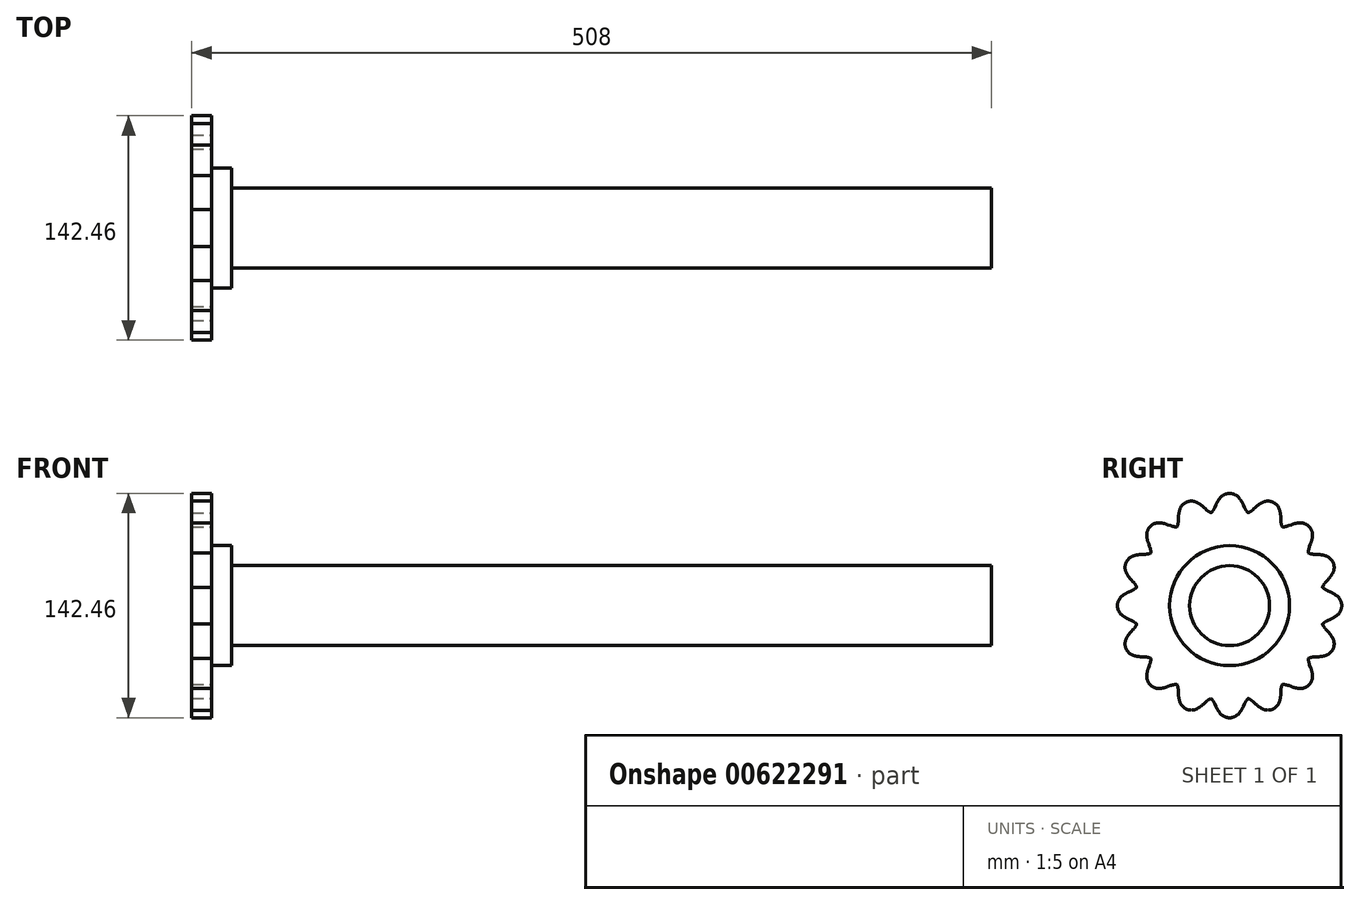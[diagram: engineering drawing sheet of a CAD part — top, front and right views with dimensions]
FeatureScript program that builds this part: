
annotation { "Feature Type Name" : "Feature", "Feature Type Description" : "" }
export const myFeature = defineFeature(function(context is Context, id is Id, definition is map)
    precondition{}
    {
        {
            var Q0;
            Q0=qCreatedBy(makeId("Front.planeOp"),FACE);
            var sketch = newSketch(context, id + "F0", { "sketchPlane" : qUnion([Q0])});
            skLineSegment(sketch, "E0", {"start": v(0, 0) * mm, "end": v(55.03, 0) * mm, "construction": true});
            skLineSegment(sketch, "E1.bottom", {"start": v(0, 25.4) * mm, "end": v(12.7, 25.4) * mm});
            skLineSegment(sketch, "E1.top", {"start": v(0, 76.2) * mm, "end": v(12.7, 76.2) * mm});
            skLineSegment(sketch, "E1.left", {"start": v(0, 25.4) * mm, "end": v(0, 76.2) * mm});
            skLineSegment(sketch, "E1.right", {"start": v(12.7, 25.4) * mm, "end": v(12.7, 76.2) * mm});
            skLineSegment(sketch, "E2.MirrorCS", {"start": v(12.7, -25.4) * mm, "end": v(12.7, -76.2) * mm});
            skLineSegment(sketch, "E3.MirrorCS", {"start": v(0, -25.4) * mm, "end": v(0, -76.2) * mm});
            skLineSegment(sketch, "E4.MirrorCS", {"start": v(0, -76.2) * mm, "end": v(12.7, -76.2) * mm});
            skLineSegment(sketch, "E5.MirrorCS", {"start": v(0, -25.4) * mm, "end": v(12.7, -25.4) * mm});
            skLineSegment(sketch, "E6.bottom", {"start": v(0, 38.1) * mm, "end": v(25.4, 38.1) * mm});
            skLineSegment(sketch, "E6.top", {"start": v(0, 25.4) * mm, "end": v(25.4, 25.4) * mm});
            skLineSegment(sketch, "E6.left", {"start": v(0, 38.1) * mm, "end": v(0, 25.4) * mm});
            skLineSegment(sketch, "E6.right", {"start": v(25.4, 38.1) * mm, "end": v(25.4, 25.4) * mm});
            skLineSegment(sketch, "E7.MirrorCS", {"start": v(25.4, -38.1) * mm, "end": v(25.4, -25.4) * mm});
            skLineSegment(sketch, "E8.MirrorCS", {"start": v(0, -38.1) * mm, "end": v(0, -25.4) * mm});
            skLineSegment(sketch, "E9.MirrorCS", {"start": v(0, -25.4) * mm, "end": v(25.4, -25.4) * mm});
            skLineSegment(sketch, "E10.MirrorCS", {"start": v(0, -38.1) * mm, "end": v(25.4, -38.1) * mm});
            skSolve(sketch);
        }
        {
            var Q0;
            Q0=qSketchRegion(id+"F0",true);
            var Q1;
            Q1=sQuery(id+"F0.wireOp",EDGE,"E0");
            revolve(context, id + "F1", {"entities" : qUnion([Q0]), "axis" : qUnion([Q1]), "revolveType" : RevolveType.FULL});
        }
        {
            var Q0;
            Q0=makeQuery(id+"F1.opRevolve","SWEPT_FACE",FACE,{"disambiguationData":[OSD([sQuery(id+"F0.wireOp",EDGE,"E3.MirrorCS"),sQuery(id+"F0.wireOp",EDGE,"E8.MirrorCS")])]});
            var sketch = newSketch(context, id + "F2", { "sketchPlane" : qUnion([Q0])});
            skCircle(sketch, "E11", {"center": v(0, 0) * mm, "radius": 25.4 * mm});
            skSolve(sketch);
        }
        {
            var Q0;
            Q0=makeQuery(id+"F2.imprint","IMPRINT",FACE,{"disambiguationData":[TD([[makeQuery(id+"F2.imprint","IMPRINT",EDGE,{"derivedFrom":sQuery(id+"F2.wireOp",EDGE,"E11")}),1.0]])]});
            extrude(context, id + "F3", {"entities" : qUnion([Q0]), "oppositeDirection" : true, "depth" : 508 * mm, "offsetDistance" : 25.4 * mm});
        }
        {
            var Q0;
            Q0=makeQuery(id+"F3.opExtrude","SWEPT_BODY",BODY,{"disambiguationData":[OSD([sQuery(id+"F2.wireOp",EDGE,"E11")])]});
            var Q1;
            Q1=makeQuery(id+"F1.opRevolve","SWEPT_BODY",BODY,{"disambiguationData":[OSD([sQuery(id+"F0.wireOp",EDGE,"E2.MirrorCS"),sQuery(id+"F0.wireOp",EDGE,"E3.MirrorCS"),sQuery(id+"F0.wireOp",EDGE,"E4.MirrorCS"),sQuery(id+"F0.wireOp",EDGE,"E7.MirrorCS"),sQuery(id+"F0.wireOp",EDGE,"E8.MirrorCS"),sQuery(id+"F0.wireOp",EDGE,"E9.MirrorCS"),sQuery(id+"F0.wireOp",EDGE,"E10.MirrorCS")])]});
            var Q2;
            Q2=makeQuery(id+"F1.opRevolve","SWEPT_BODY",BODY,{"disambiguationData":[OSD([sQuery(id+"F0.wireOp",EDGE,"E6.bottom"),sQuery(id+"F0.wireOp",EDGE,"E6.top"),sQuery(id+"F0.wireOp",EDGE,"E6.right"),sQuery(id+"F0.wireOp",EDGE,"E1.bottom"),sQuery(id+"F0.wireOp",EDGE,"E1.top"),sQuery(id+"F0.wireOp",EDGE,"E1.left"),sQuery(id+"F0.wireOp",EDGE,"E1.right")])]});
            booleanBodies(context, id + "F4", {"operationType" : BooleanOperationType.UNION, "tools" : qUnion([Q0, Q1, Q2])});
        }
        {
            var Q0;
            Q0=makeQuery(id+"F4.opBoolean","MERGE",FACE,{"derivedFrom":[makeQuery(id+"F1.opRevolve","SWEPT_FACE",FACE,{"disambiguationData":[OSD([sQuery(id+"F0.wireOp",EDGE,"E3.MirrorCS"),sQuery(id+"F0.wireOp",EDGE,"E8.MirrorCS")])]}),makeQuery(id+"F3.opExtrude","CAP_FACE",FACE,{"disambiguationData":[OSD([sQuery(id+"F2.wireOp",EDGE,"E11")])],"isStart":true})]});
            var sketch = newSketch(context, id + "F5", { "sketchPlane" : qUnion([Q0])});
            skLineSegment(sketch, "E12", {"start": v(0, 63.5) * mm, "end": v(-36.63, 63.5) * mm, "construction": true});
            skLineSegment(sketch, "E13", {"start": v(-36.63, 63.5) * mm, "end": v(0, 63.5) * mm, "construction": true});
            skLineSegment(sketch, "E14", {"start": v(0, 63.5) * mm, "end": v(-9.74, 55.68) * mm, "construction": true});
            skLineSegment(sketch, "E15", {"start": v(-9.74, 55.68) * mm, "end": v(8.7, 63.99) * mm, "construction": true});
            skLineSegment(sketch, "E16", {"start": v(8.7, 63.99) * mm, "end": v(9.4, 62.43) * mm});
            skArc(sketch, "E17", {"start": v(11.72, 58.93) * mm, "mid": v(31.82, 74.84) * mm, "end": v(9.4, 62.43) * mm, "construction": true});
            skLineSegment(sketch, "E18", {"start": v(-36.76, 12.49) * mm, "end": v(-36.76, 12.49) * mm});
            skArc(sketch, "E19", {"start": v(9.4, 62.43) * mm, "mid": v(10.42, 60.59) * mm, "end": v(11.72, 58.93) * mm});
            skArc(sketch, "E20", {"start": v(8.7, 63.99) * mm, "mid": v(7.5, 66.25) * mm, "end": v(6.03, 68.34) * mm});
            skArc(sketch, "E21", {"start": v(6.03, 68.34) * mm, "mid": v(-26.98, 45.12) * mm, "end": v(8.7, 63.99) * mm, "construction": true});
            skArc(sketch, "E22.MirrorCS", {"start": v(-8.7, 63.99) * mm, "mid": v(-7.5, 66.25) * mm, "end": v(-6.03, 68.34) * mm});
            skLineSegment(sketch, "E23.MirrorCS", {"start": v(-8.7, 63.99) * mm, "end": v(-9.4, 62.43) * mm});
            skArc(sketch, "E24", {"start": v(6.03, 68.34) * mm, "mid": v(0, 71.23) * mm, "end": v(-6.03, 68.34) * mm});
            skArc(sketch, "E25", {"start": v(-6.03, 68.34) * mm, "mid": v(0, 55.77) * mm, "end": v(6.03, 68.34) * mm, "construction": true});
            skLineSegment(sketch, "E26", {"start": v(0, 63.5) * mm, "end": v(0, 0) * mm, "construction": true});
            skLineSegment(sketch, "E27", {"start": v(0, 0) * mm, "end": v(11.72, 58.93) * mm, "construction": true});
            skCircle(sketch, "E28", {"center": v(0, 0) * mm, "radius": 63.5 * mm, "construction": true});
            skArc(sketch, "E29.MirrorCS", {"start": v(-9.4, 62.43) * mm, "mid": v(-10.42, 60.59) * mm, "end": v(-11.72, 58.93) * mm});
            skLineSegment(sketch, "E30.1.0", {"start": v(-32.52, 55.79) * mm, "end": v(-32.57, 54.08) * mm});
            skArc(sketch, "E30.1.1", {"start": v(-32.57, 54.08) * mm, "mid": v(-32.8, 51.99) * mm, "end": v(-33.38, 49.96) * mm});
            skArc(sketch, "E30.1.2", {"start": v(-32.52, 55.79) * mm, "mid": v(-32.28, 58.33) * mm, "end": v(-31.72, 60.83) * mm});
            skArc(sketch, "E30.1.3", {"start": v(-20.58, 65.44) * mm, "mid": v(-27.26, 65.8) * mm, "end": v(-31.72, 60.83) * mm});
            skArc(sketch, "E30.1.4", {"start": v(-16.45, 62.44) * mm, "mid": v(-18.42, 64.07) * mm, "end": v(-20.58, 65.44) * mm});
            skArc(sketch, "E30.1.5", {"start": v(-15.21, 61.27) * mm, "mid": v(-13.56, 59.96) * mm, "end": v(-11.72, 58.93) * mm});
            skLineSegment(sketch, "E30.1.6", {"start": v(-16.45, 62.44) * mm, "end": v(-15.21, 61.27) * mm});
            skLineSegment(sketch, "E30.2.0", {"start": v(-51.4, 39.1) * mm, "end": v(-50.79, 37.5) * mm});
            skArc(sketch, "E30.2.1", {"start": v(-50.79, 37.5) * mm, "mid": v(-50.2, 35.48) * mm, "end": v(-49.96, 33.38) * mm});
            skArc(sketch, "E30.2.2", {"start": v(-51.4, 39.1) * mm, "mid": v(-52.15, 41.54) * mm, "end": v(-52.59, 44.06) * mm});
            skArc(sketch, "E30.2.3", {"start": v(-44.06, 52.59) * mm, "mid": v(-50.37, 50.37) * mm, "end": v(-52.59, 44.06) * mm});
            skArc(sketch, "E30.2.4", {"start": v(-39.1, 51.4) * mm, "mid": v(-41.54, 52.15) * mm, "end": v(-44.06, 52.59) * mm});
            skArc(sketch, "E30.2.5", {"start": v(-37.5, 50.79) * mm, "mid": v(-35.48, 50.2) * mm, "end": v(-33.38, 49.96) * mm});
            skLineSegment(sketch, "E30.2.6", {"start": v(-39.1, 51.4) * mm, "end": v(-37.5, 50.79) * mm});
            skLineSegment(sketch, "E31.2.3.0", {"start": v(-62.44, 16.45) * mm, "end": v(-61.27, 15.21) * mm});
            skArc(sketch, "E31.3.3.0", {"start": v(-61.27, 15.21) * mm, "mid": v(-59.96, 13.56) * mm, "end": v(-58.93, 11.72) * mm});
            skArc(sketch, "E31.7.3.0", {"start": v(-62.44, 16.45) * mm, "mid": v(-64.07, 18.42) * mm, "end": v(-65.44, 20.58) * mm});
            skArc(sketch, "E31.11.3.0", {"start": v(-60.83, 31.72) * mm, "mid": v(-65.8, 27.26) * mm, "end": v(-65.44, 20.58) * mm});
            skArc(sketch, "E31.15.3.0", {"start": v(-55.79, 32.52) * mm, "mid": v(-58.33, 32.28) * mm, "end": v(-60.83, 31.72) * mm});
            skArc(sketch, "E31.19.3.0", {"start": v(-54.08, 32.57) * mm, "mid": v(-51.99, 32.8) * mm, "end": v(-49.96, 33.38) * mm});
            skLineSegment(sketch, "E31.23.3.0", {"start": v(-55.79, 32.52) * mm, "end": v(-54.08, 32.57) * mm});
            skLineSegment(sketch, "E31.2.4.0", {"start": v(-63.99, -8.7) * mm, "end": v(-62.43, -9.4) * mm});
            skArc(sketch, "E31.3.4.0", {"start": v(-62.43, -9.4) * mm, "mid": v(-60.59, -10.42) * mm, "end": v(-58.93, -11.72) * mm});
            skArc(sketch, "E31.7.4.0", {"start": v(-63.99, -8.7) * mm, "mid": v(-66.25, -7.5) * mm, "end": v(-68.34, -6.03) * mm});
            skArc(sketch, "E31.11.4.0", {"start": v(-68.34, 6.03) * mm, "mid": v(-71.23, 0) * mm, "end": v(-68.34, -6.03) * mm});
            skArc(sketch, "E31.15.4.0", {"start": v(-63.99, 8.7) * mm, "mid": v(-66.25, 7.5) * mm, "end": v(-68.34, 6.03) * mm});
            skArc(sketch, "E31.19.4.0", {"start": v(-62.43, 9.4) * mm, "mid": v(-60.59, 10.42) * mm, "end": v(-58.93, 11.72) * mm});
            skLineSegment(sketch, "E31.23.4.0", {"start": v(-63.99, 8.7) * mm, "end": v(-62.43, 9.4) * mm});
            skLineSegment(sketch, "E31.2.5.0", {"start": v(-55.79, -32.52) * mm, "end": v(-54.08, -32.57) * mm});
            skArc(sketch, "E31.3.5.0", {"start": v(-54.08, -32.57) * mm, "mid": v(-51.99, -32.8) * mm, "end": v(-49.96, -33.38) * mm});
            skArc(sketch, "E31.7.5.0", {"start": v(-55.79, -32.52) * mm, "mid": v(-58.33, -32.28) * mm, "end": v(-60.83, -31.72) * mm});
            skArc(sketch, "E31.11.5.0", {"start": v(-65.44, -20.58) * mm, "mid": v(-65.8, -27.26) * mm, "end": v(-60.83, -31.72) * mm});
            skArc(sketch, "E31.15.5.0", {"start": v(-62.44, -16.45) * mm, "mid": v(-64.07, -18.42) * mm, "end": v(-65.44, -20.58) * mm});
            skArc(sketch, "E31.19.5.0", {"start": v(-61.27, -15.21) * mm, "mid": v(-59.96, -13.56) * mm, "end": v(-58.93, -11.72) * mm});
            skLineSegment(sketch, "E31.23.5.0", {"start": v(-62.44, -16.45) * mm, "end": v(-61.27, -15.21) * mm});
            skLineSegment(sketch, "E31.2.6.0", {"start": v(-39.1, -51.4) * mm, "end": v(-37.5, -50.79) * mm});
            skArc(sketch, "E31.3.6.0", {"start": v(-37.5, -50.79) * mm, "mid": v(-35.48, -50.2) * mm, "end": v(-33.38, -49.96) * mm});
            skArc(sketch, "E31.7.6.0", {"start": v(-39.1, -51.4) * mm, "mid": v(-41.54, -52.15) * mm, "end": v(-44.06, -52.59) * mm});
            skArc(sketch, "E31.11.6.0", {"start": v(-52.59, -44.06) * mm, "mid": v(-50.37, -50.37) * mm, "end": v(-44.06, -52.59) * mm});
            skArc(sketch, "E31.15.6.0", {"start": v(-51.4, -39.1) * mm, "mid": v(-52.15, -41.54) * mm, "end": v(-52.59, -44.06) * mm});
            skArc(sketch, "E31.19.6.0", {"start": v(-50.79, -37.5) * mm, "mid": v(-50.2, -35.48) * mm, "end": v(-49.96, -33.38) * mm});
            skLineSegment(sketch, "E31.23.6.0", {"start": v(-51.4, -39.1) * mm, "end": v(-50.79, -37.5) * mm});
            skLineSegment(sketch, "E31.2.7.0", {"start": v(-16.45, -62.44) * mm, "end": v(-15.21, -61.27) * mm});
            skArc(sketch, "E31.3.7.0", {"start": v(-15.21, -61.27) * mm, "mid": v(-13.56, -59.96) * mm, "end": v(-11.72, -58.93) * mm});
            skArc(sketch, "E31.7.7.0", {"start": v(-16.45, -62.44) * mm, "mid": v(-18.42, -64.07) * mm, "end": v(-20.58, -65.44) * mm});
            skArc(sketch, "E31.11.7.0", {"start": v(-31.72, -60.83) * mm, "mid": v(-27.26, -65.8) * mm, "end": v(-20.58, -65.44) * mm});
            skArc(sketch, "E31.15.7.0", {"start": v(-32.52, -55.79) * mm, "mid": v(-32.28, -58.33) * mm, "end": v(-31.72, -60.83) * mm});
            skArc(sketch, "E31.19.7.0", {"start": v(-32.57, -54.08) * mm, "mid": v(-32.8, -51.99) * mm, "end": v(-33.38, -49.96) * mm});
            skLineSegment(sketch, "E31.23.7.0", {"start": v(-32.52, -55.79) * mm, "end": v(-32.57, -54.08) * mm});
            skLineSegment(sketch, "E31.2.8.0", {"start": v(8.7, -63.99) * mm, "end": v(9.4, -62.43) * mm});
            skArc(sketch, "E31.3.8.0", {"start": v(9.4, -62.43) * mm, "mid": v(10.42, -60.59) * mm, "end": v(11.72, -58.93) * mm});
            skArc(sketch, "E31.7.8.0", {"start": v(8.7, -63.99) * mm, "mid": v(7.5, -66.25) * mm, "end": v(6.03, -68.34) * mm});
            skArc(sketch, "E31.11.8.0", {"start": v(-6.03, -68.34) * mm, "mid": v(0, -71.23) * mm, "end": v(6.03, -68.34) * mm});
            skArc(sketch, "E31.15.8.0", {"start": v(-8.7, -63.99) * mm, "mid": v(-7.5, -66.25) * mm, "end": v(-6.03, -68.34) * mm});
            skArc(sketch, "E31.19.8.0", {"start": v(-9.4, -62.43) * mm, "mid": v(-10.42, -60.59) * mm, "end": v(-11.72, -58.93) * mm});
            skLineSegment(sketch, "E31.23.8.0", {"start": v(-8.7, -63.99) * mm, "end": v(-9.4, -62.43) * mm});
            skLineSegment(sketch, "E31.2.9.0", {"start": v(32.52, -55.79) * mm, "end": v(32.57, -54.08) * mm});
            skArc(sketch, "E31.3.9.0", {"start": v(32.57, -54.08) * mm, "mid": v(32.8, -51.99) * mm, "end": v(33.38, -49.96) * mm});
            skArc(sketch, "E31.7.9.0", {"start": v(32.52, -55.79) * mm, "mid": v(32.28, -58.33) * mm, "end": v(31.72, -60.83) * mm});
            skArc(sketch, "E31.11.9.0", {"start": v(20.58, -65.44) * mm, "mid": v(27.26, -65.8) * mm, "end": v(31.72, -60.83) * mm});
            skArc(sketch, "E31.15.9.0", {"start": v(16.45, -62.44) * mm, "mid": v(18.42, -64.07) * mm, "end": v(20.58, -65.44) * mm});
            skArc(sketch, "E31.19.9.0", {"start": v(15.21, -61.27) * mm, "mid": v(13.56, -59.96) * mm, "end": v(11.72, -58.93) * mm});
            skLineSegment(sketch, "E31.23.9.0", {"start": v(16.45, -62.44) * mm, "end": v(15.21, -61.27) * mm});
            skLineSegment(sketch, "E31.2.10.0", {"start": v(51.4, -39.1) * mm, "end": v(50.79, -37.5) * mm});
            skArc(sketch, "E31.3.10.0", {"start": v(50.79, -37.5) * mm, "mid": v(50.2, -35.48) * mm, "end": v(49.96, -33.38) * mm});
            skArc(sketch, "E31.7.10.0", {"start": v(51.4, -39.1) * mm, "mid": v(52.15, -41.54) * mm, "end": v(52.59, -44.06) * mm});
            skArc(sketch, "E31.11.10.0", {"start": v(44.06, -52.59) * mm, "mid": v(50.37, -50.37) * mm, "end": v(52.59, -44.06) * mm});
            skArc(sketch, "E31.15.10.0", {"start": v(39.1, -51.4) * mm, "mid": v(41.54, -52.15) * mm, "end": v(44.06, -52.59) * mm});
            skArc(sketch, "E31.19.10.0", {"start": v(37.5, -50.79) * mm, "mid": v(35.48, -50.2) * mm, "end": v(33.38, -49.96) * mm});
            skLineSegment(sketch, "E31.23.10.0", {"start": v(39.1, -51.4) * mm, "end": v(37.5, -50.79) * mm});
            skLineSegment(sketch, "E31.2.11.0", {"start": v(62.44, -16.45) * mm, "end": v(61.27, -15.21) * mm});
            skArc(sketch, "E31.3.11.0", {"start": v(61.27, -15.21) * mm, "mid": v(59.96, -13.56) * mm, "end": v(58.93, -11.72) * mm});
            skArc(sketch, "E31.7.11.0", {"start": v(62.44, -16.45) * mm, "mid": v(64.07, -18.42) * mm, "end": v(65.44, -20.58) * mm});
            skArc(sketch, "E31.11.11.0", {"start": v(60.83, -31.72) * mm, "mid": v(65.8, -27.26) * mm, "end": v(65.44, -20.58) * mm});
            skArc(sketch, "E31.15.11.0", {"start": v(55.79, -32.52) * mm, "mid": v(58.33, -32.28) * mm, "end": v(60.83, -31.72) * mm});
            skArc(sketch, "E31.19.11.0", {"start": v(54.08, -32.57) * mm, "mid": v(51.99, -32.8) * mm, "end": v(49.96, -33.38) * mm});
            skLineSegment(sketch, "E31.23.11.0", {"start": v(55.79, -32.52) * mm, "end": v(54.08, -32.57) * mm});
            skLineSegment(sketch, "E31.2.12.0", {"start": v(63.99, 8.7) * mm, "end": v(62.43, 9.4) * mm});
            skArc(sketch, "E31.3.12.0", {"start": v(62.43, 9.4) * mm, "mid": v(60.59, 10.42) * mm, "end": v(58.93, 11.72) * mm});
            skArc(sketch, "E31.7.12.0", {"start": v(63.99, 8.7) * mm, "mid": v(66.25, 7.5) * mm, "end": v(68.34, 6.03) * mm});
            skArc(sketch, "E31.11.12.0", {"start": v(68.34, -6.03) * mm, "mid": v(71.23, 0) * mm, "end": v(68.34, 6.03) * mm});
            skArc(sketch, "E31.15.12.0", {"start": v(63.99, -8.7) * mm, "mid": v(66.25, -7.5) * mm, "end": v(68.34, -6.03) * mm});
            skArc(sketch, "E31.19.12.0", {"start": v(62.43, -9.4) * mm, "mid": v(60.59, -10.42) * mm, "end": v(58.93, -11.72) * mm});
            skLineSegment(sketch, "E31.23.12.0", {"start": v(63.99, -8.7) * mm, "end": v(62.43, -9.4) * mm});
            skLineSegment(sketch, "E31.2.13.0", {"start": v(55.79, 32.52) * mm, "end": v(54.08, 32.57) * mm});
            skArc(sketch, "E31.3.13.0", {"start": v(54.08, 32.57) * mm, "mid": v(51.99, 32.8) * mm, "end": v(49.96, 33.38) * mm});
            skArc(sketch, "E31.7.13.0", {"start": v(55.79, 32.52) * mm, "mid": v(58.33, 32.28) * mm, "end": v(60.83, 31.72) * mm});
            skArc(sketch, "E31.11.13.0", {"start": v(65.44, 20.58) * mm, "mid": v(65.8, 27.26) * mm, "end": v(60.83, 31.72) * mm});
            skArc(sketch, "E31.15.13.0", {"start": v(62.44, 16.45) * mm, "mid": v(64.07, 18.42) * mm, "end": v(65.44, 20.58) * mm});
            skArc(sketch, "E31.19.13.0", {"start": v(61.27, 15.21) * mm, "mid": v(59.96, 13.56) * mm, "end": v(58.93, 11.72) * mm});
            skLineSegment(sketch, "E31.23.13.0", {"start": v(62.44, 16.45) * mm, "end": v(61.27, 15.21) * mm});
            skLineSegment(sketch, "E31.2.14.0", {"start": v(39.1, 51.4) * mm, "end": v(37.5, 50.79) * mm});
            skArc(sketch, "E31.3.14.0", {"start": v(37.5, 50.79) * mm, "mid": v(35.48, 50.2) * mm, "end": v(33.38, 49.96) * mm});
            skArc(sketch, "E31.7.14.0", {"start": v(39.1, 51.4) * mm, "mid": v(41.54, 52.15) * mm, "end": v(44.06, 52.59) * mm});
            skArc(sketch, "E31.11.14.0", {"start": v(52.59, 44.06) * mm, "mid": v(50.37, 50.37) * mm, "end": v(44.06, 52.59) * mm});
            skArc(sketch, "E31.15.14.0", {"start": v(51.4, 39.1) * mm, "mid": v(52.15, 41.54) * mm, "end": v(52.59, 44.06) * mm});
            skArc(sketch, "E31.19.14.0", {"start": v(50.79, 37.5) * mm, "mid": v(50.2, 35.48) * mm, "end": v(49.96, 33.38) * mm});
            skLineSegment(sketch, "E31.23.14.0", {"start": v(51.4, 39.1) * mm, "end": v(50.79, 37.5) * mm});
            skLineSegment(sketch, "E31.2.15.0", {"start": v(16.45, 62.44) * mm, "end": v(15.21, 61.27) * mm});
            skArc(sketch, "E31.3.15.0", {"start": v(15.21, 61.27) * mm, "mid": v(13.56, 59.96) * mm, "end": v(11.72, 58.93) * mm});
            skArc(sketch, "E31.7.15.0", {"start": v(16.45, 62.44) * mm, "mid": v(18.42, 64.07) * mm, "end": v(20.58, 65.44) * mm});
            skArc(sketch, "E31.11.15.0", {"start": v(31.72, 60.83) * mm, "mid": v(27.26, 65.8) * mm, "end": v(20.58, 65.44) * mm});
            skArc(sketch, "E31.15.15.0", {"start": v(32.52, 55.79) * mm, "mid": v(32.28, 58.33) * mm, "end": v(31.72, 60.83) * mm});
            skArc(sketch, "E31.19.15.0", {"start": v(32.57, 54.08) * mm, "mid": v(32.8, 51.99) * mm, "end": v(33.38, 49.96) * mm});
            skLineSegment(sketch, "E31.23.15.0", {"start": v(32.52, 55.79) * mm, "end": v(32.57, 54.08) * mm});
            skSolve(sketch);
        }
        {
            var Q0;
            Q0=qSketchRegion(id+"F5",true);
            extrude(context, id + "F6", {"entities" : qUnion([Q0]), "operationType" : NewBodyOperationType.INTERSECT, "endBound" : BoundingType.THROUGH_ALL, "oppositeDirection" : true, "depth" : 25.4 * mm, "offsetDistance" : 25.4 * mm});
        }
    });
